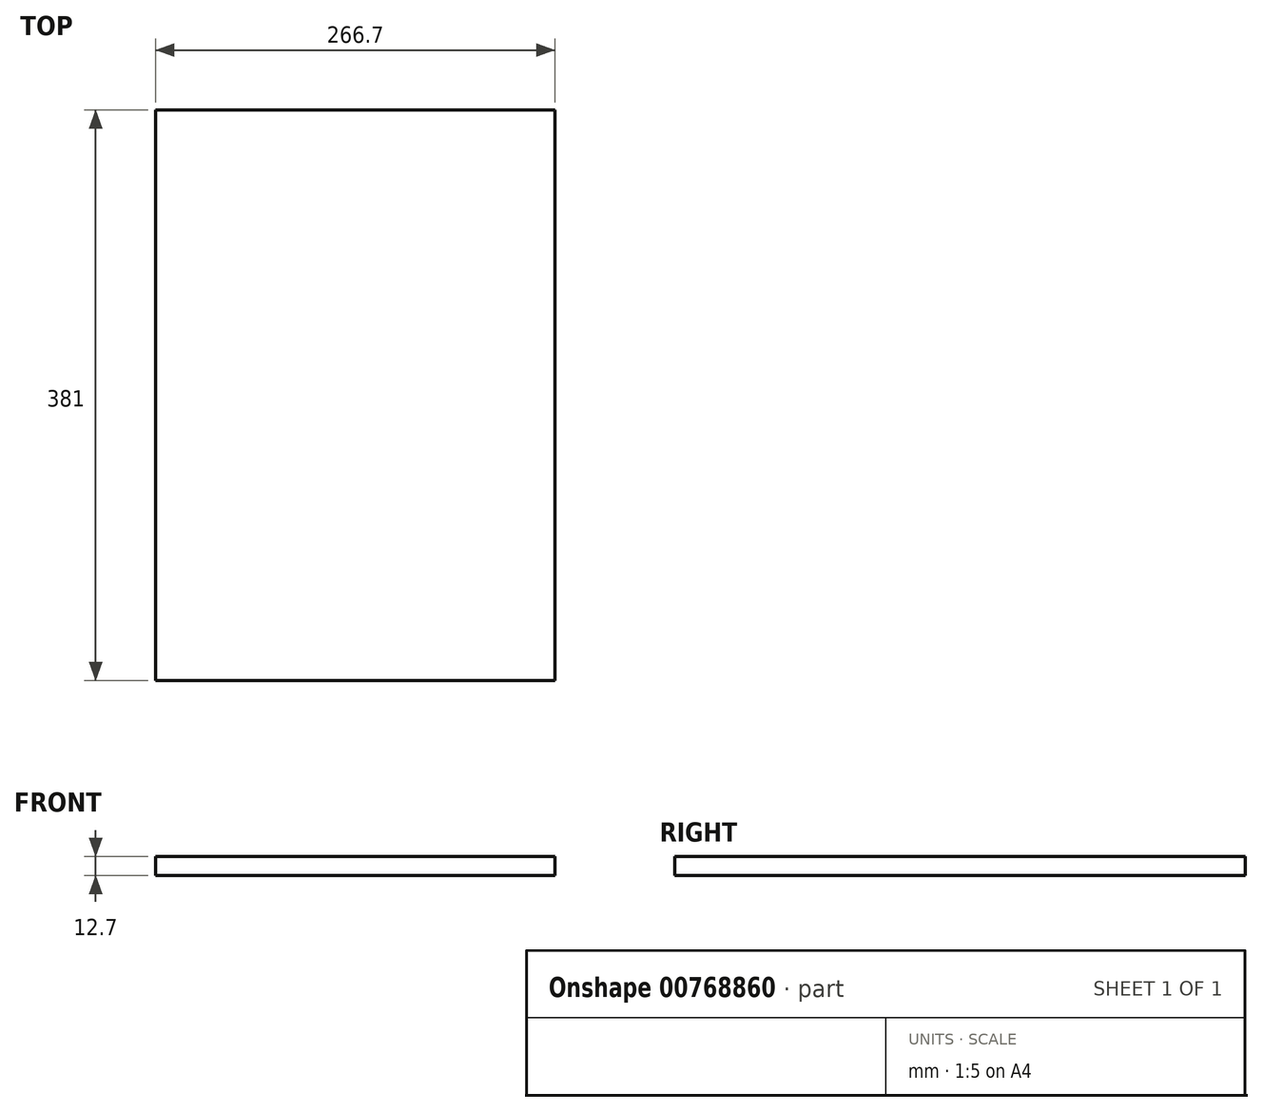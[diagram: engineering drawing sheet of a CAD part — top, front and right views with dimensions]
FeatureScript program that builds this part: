
annotation { "Feature Type Name" : "Feature", "Feature Type Description" : "" }
export const myFeature = defineFeature(function(context is Context, id is Id, definition is map)
    precondition{}
    {
        {
            var Q0;
            Q0=qCreatedBy(makeId("Front.planeOp"),FACE);
            var sketch = newSketch(context, id + "F0", { "sketchPlane" : qUnion([Q0])});
            skLineSegment(sketch, "E0.bottom", {"start": v(-133.35, 6.35) * mm, "end": v(133.35, 6.35) * mm});
            skLineSegment(sketch, "E0.top", {"start": v(-133.35, -6.35) * mm, "end": v(133.35, -6.35) * mm});
            skLineSegment(sketch, "E0.left", {"start": v(-133.35, 6.35) * mm, "end": v(-133.35, -6.35) * mm});
            skLineSegment(sketch, "E0.right", {"start": v(133.35, 6.35) * mm, "end": v(133.35, -6.35) * mm});
            skPoint(sketch, "E0.middle", {"position": v(0, 0) * mm});
            skSolve(sketch);
        }
        {
            var Q0;
            Q0=makeQuery(id+"F0.imprint","IMPRINT",FACE,{"disambiguationData":[TD([[makeQuery(id+"F0.imprint","IMPRINT",EDGE,{"derivedFrom":sQuery(id+"F0.wireOp",EDGE,"E0.bottom")}),-1.0]])]});
            extrude(context, id + "F1", {"entities" : qUnion([Q0]), "depth" : 381 * mm, "offsetDistance" : 25.4 * mm});
        }
    });
